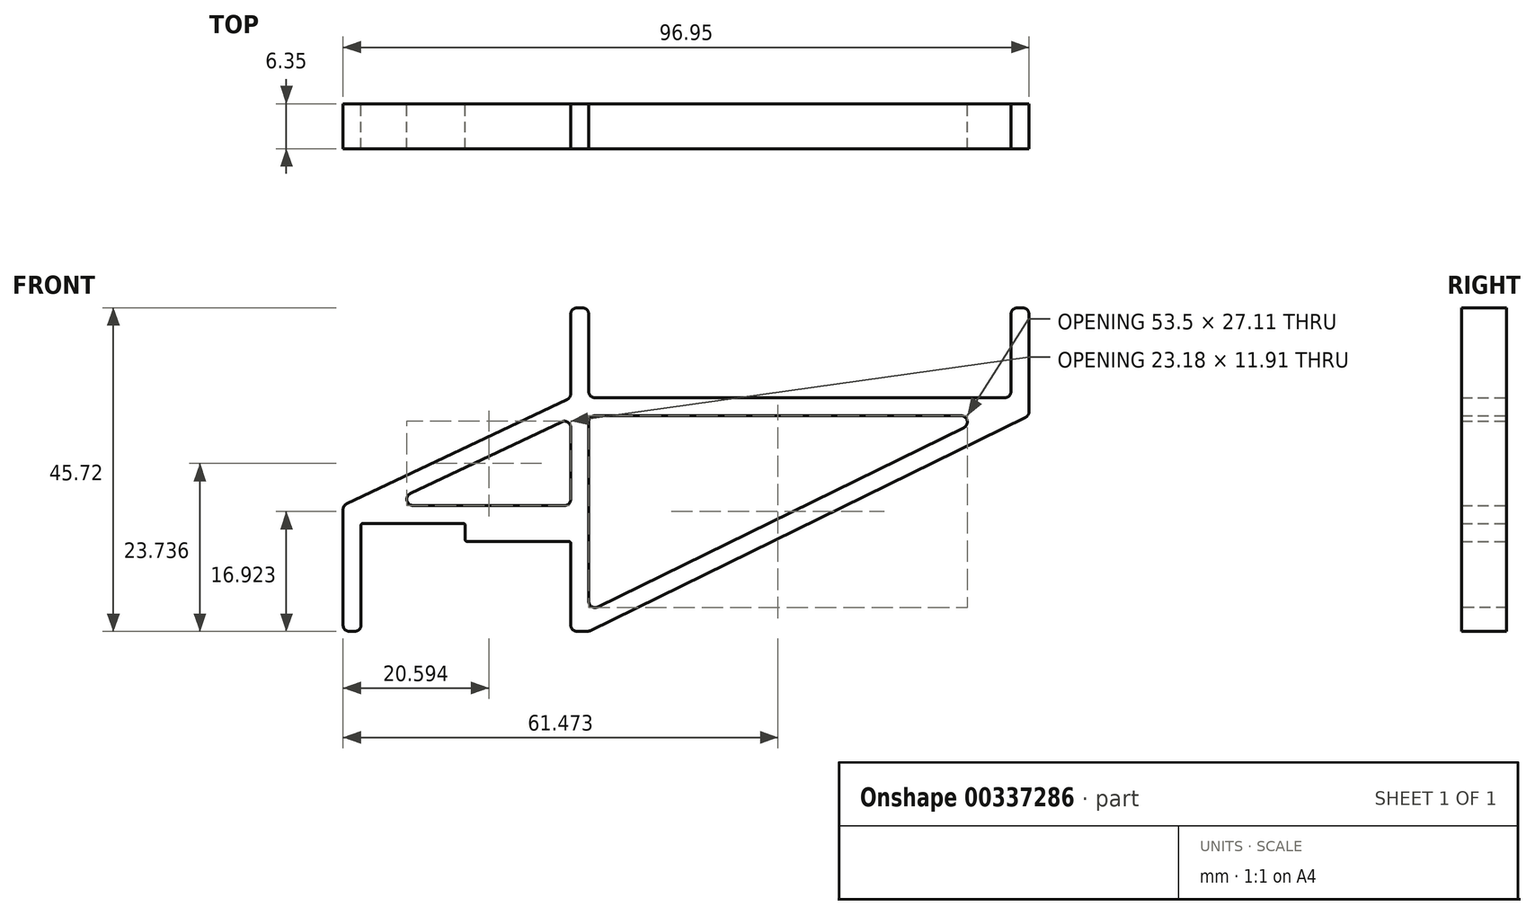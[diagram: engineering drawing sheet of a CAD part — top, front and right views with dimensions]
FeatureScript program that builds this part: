
annotation { "Feature Type Name" : "Feature", "Feature Type Description" : "" }
export const myFeature = defineFeature(function(context is Context, id is Id, definition is map)
    precondition{}
    {
        {
            var Q0;
            Q0=qCreatedBy(makeId("Front.planeOp"),FACE);
            var sketch = newSketch(context, id + "F0", { "sketchPlane" : qUnion([Q0])});
            skLineSegment(sketch, "E0", {"start": v(2.54, 17.78) * mm, "end": v(2.54, 15.24) * mm});
            skLineSegment(sketch, "E1", {"start": v(2.54, 15.24) * mm, "end": v(32.18, 15.24) * mm});
            skLineSegment(sketch, "E2", {"start": v(17.27, 15.24) * mm, "end": v(17.27, 12.7) * mm});
            skLineSegment(sketch, "E3", {"start": v(2.54, 17.78) * mm, "end": v(32.18, 17.78) * mm});
            skLineSegment(sketch, "E4", {"start": v(17.27, 12.7) * mm, "end": v(32.18, 12.7) * mm});
            skLineSegment(sketch, "E5", {"start": v(32.18, 12.7) * mm, "end": v(32.18, 17.78) * mm});
            skLineSegment(sketch, "E6", {"start": v(32.18, 17.78) * mm, "end": v(34.72, 17.78) * mm});
            skLineSegment(sketch, "E7", {"start": v(34.72, 17.78) * mm, "end": v(34.72, 0) * mm});
            skLineSegment(sketch, "E8", {"start": v(32.18, 12.7) * mm, "end": v(32.18, 0) * mm});
            skLineSegment(sketch, "E9", {"start": v(2.54, 17.78) * mm, "end": v(0, 17.78) * mm});
            skLineSegment(sketch, "E10", {"start": v(2.54, 15.24) * mm, "end": v(2.54, 0) * mm});
            skLineSegment(sketch, "E11", {"start": v(0, 17.78) * mm, "end": v(0, 0) * mm});
            skLineSegment(sketch, "E12", {"start": v(0, 0) * mm, "end": v(2.54, 0) * mm});
            skLineSegment(sketch, "E13", {"start": v(34.72, 17.78) * mm, "end": v(34.72, 13.97) * mm});
            skLineSegment(sketch, "E14", {"start": v(32.18, 0) * mm, "end": v(34.72, 0) * mm});
            skLineSegment(sketch, "E15", {"start": v(32.18, 17.78) * mm, "end": v(32.18, 20.32) * mm});
            skLineSegment(sketch, "E16", {"start": v(32.18, 20.32) * mm, "end": v(32.18, 33.02) * mm});
            skLineSegment(sketch, "E17", {"start": v(32.18, 33.02) * mm, "end": v(34.72, 33.02) * mm});
            skLineSegment(sketch, "E18", {"start": v(0, 17.78) * mm, "end": v(32.18, 33.02) * mm});
            skLineSegment(sketch, "E19", {"start": v(5.93, 17.78) * mm, "end": v(32.18, 30.2) * mm});
            skLineSegment(sketch, "E20", {"start": v(34.72, 33.02) * mm, "end": v(34.72, 17.78) * mm});
            skLineSegment(sketch, "E21", {"start": v(34.72, 33.02) * mm, "end": v(96.95, 33.02) * mm});
            skLineSegment(sketch, "E22", {"start": v(96.95, 33.02) * mm, "end": v(96.95, 30.48) * mm});
            skLineSegment(sketch, "E23", {"start": v(34.72, 30.48) * mm, "end": v(96.95, 30.48) * mm});
            skLineSegment(sketch, "E24", {"start": v(32.18, 33.02) * mm, "end": v(32.18, 45.72) * mm});
            skLineSegment(sketch, "E25", {"start": v(32.18, 45.72) * mm, "end": v(34.72, 45.72) * mm});
            skLineSegment(sketch, "E26", {"start": v(34.72, 33.02) * mm, "end": v(34.72, 45.72) * mm});
            skLineSegment(sketch, "E27", {"start": v(96.95, 33.02) * mm, "end": v(96.95, 45.72) * mm});
            skLineSegment(sketch, "E28", {"start": v(96.95, 45.72) * mm, "end": v(94.41, 45.72) * mm});
            skLineSegment(sketch, "E29", {"start": v(94.41, 45.72) * mm, "end": v(94.41, 33.02) * mm});
            skLineSegment(sketch, "E30", {"start": v(34.72, 0) * mm, "end": v(96.95, 30.48) * mm});
            skLineSegment(sketch, "E31", {"start": v(34.72, 2.83) * mm, "end": v(91.18, 30.48) * mm});
            skSolve(sketch);
        }
        {
            var Q0;
            {var subQ0=sQuery(id+"F0.wireOp",EDGE,"jvLbMz3n-FQXq-gv2P-DcQT-8QfjgkFX3igj");Q0=makeQuery(id+"F0.imprint","IMPRINT",FACE,{"disambiguationData":[TD([[makeQuery(id+"F0.imprint","IMPRINT",EDGE,{"derivedFrom":subQ0}),1.0]])]});}
            var Q1;
            {var subQ4=sQuery(id+"F0.wireOp",EDGE,"E6");Q1=makeQuery(id+"F0.imprint","IMPRINT",FACE,{"disambiguationData":[TD([[makeQuery(id+"F0.imprint","IMPRINT",EDGE,{"derivedFrom":subQ4}),1.0]])]});}
            var Q2;
            {var subQ0=sQuery(id+"F0.wireOp",EDGE,"5fyH0i7X-IWu1-a1HD-RHR6-HmbiZMtqhNbi");Q2=makeQuery(id+"F0.imprint","IMPRINT",FACE,{"disambiguationData":[TD([[makeQuery(id+"F0.imprint","IMPRINT",EDGE,{"derivedFrom":subQ0}),-1.0]])]});}
            var Q3;
            {var subQ3=sQuery(id+"F0.wireOp",EDGE,"E6");Q3=makeQuery(id+"F0.imprint","IMPRINT",FACE,{"disambiguationData":[TD([[makeQuery(id+"F0.imprint","IMPRINT",EDGE,{"derivedFrom":subQ3}),-1.0]])]});}
            var Q4;
            {var subQ0=sQuery(id+"F0.wireOp",EDGE,"E17");Q4=makeQuery(id+"F0.imprint","IMPRINT",FACE,{"disambiguationData":[TD([[makeQuery(id+"F0.imprint","IMPRINT",EDGE,{"derivedFrom":subQ0}),-1.0]])]});}
            var Q5;
            {var subQ1=sQuery(id+"F0.wireOp",EDGE,"E9");Q5=makeQuery(id+"F0.imprint","IMPRINT",FACE,{"disambiguationData":[TD([[makeQuery(id+"F0.imprint","IMPRINT",EDGE,{"derivedFrom":subQ1}),-1.0]])]});}
            var Q6;
            {var subQ1=sQuery(id+"F0.wireOp",EDGE,"E0");Q6=makeQuery(id+"F0.imprint","IMPRINT",FACE,{"disambiguationData":[TD([[makeQuery(id+"F0.imprint","IMPRINT",EDGE,{"derivedFrom":subQ1}),1.0]])]});}
            var Q7;
            {var subQ3=sQuery(id+"F0.wireOp",EDGE,"E2");Q7=makeQuery(id+"F0.imprint","IMPRINT",FACE,{"disambiguationData":[TD([[makeQuery(id+"F0.imprint","IMPRINT",EDGE,{"derivedFrom":subQ3}),1.0]])]});}
            var Q8;
            Q8=makeQuery(id+"F0.imprint","IMPRINT",FACE,{"disambiguationData":[TD([[makeQuery(id+"F0.imprint","IMPRINT",EDGE,{"derivedFrom":sQuery(id+"F0.wireOp",EDGE,"E0")}),-1.0]])]});
            var Q9;
            {var subQ0=sQuery(id+"F0.wireOp",EDGE,"E30");Q9=makeQuery(id+"F0.imprint","IMPRINT",FACE,{"disambiguationData":[TD([[makeQuery(id+"F0.imprint","IMPRINT",EDGE,{"derivedFrom":subQ0}),1.0]])]});}
            var Q10;
            {var subQ0=sQuery(id+"F0.wireOp",EDGE,"E22");Q10=makeQuery(id+"F0.imprint","IMPRINT",FACE,{"disambiguationData":[TD([[makeQuery(id+"F0.imprint","IMPRINT",EDGE,{"derivedFrom":subQ0}),-1.0]])]});}
            var Q11;
            {var subQ0=sQuery(id+"F0.wireOp",EDGE,"E27");Q11=makeQuery(id+"F0.imprint","IMPRINT",FACE,{"disambiguationData":[TD([[makeQuery(id+"F0.imprint","IMPRINT",EDGE,{"derivedFrom":subQ0}),1.0]])]});}
            var Q12;
            Q12=makeQuery(id+"F0.imprint","IMPRINT",FACE,{"disambiguationData":[TD([[makeQuery(id+"F0.imprint","IMPRINT",EDGE,{"derivedFrom":sQuery(id+"F0.wireOp",EDGE,"E17")}),1.0]])]});
            extrude(context, id + "F1", {"entities" : qUnion([Q0, Q1, Q2, Q3, Q4, Q5, Q6, Q7, Q8, Q9, Q10, Q11, Q12]), "depth" : 6.35 * mm, "offsetDistance" : 25.4 * mm});
        }
        {
            var Q0;
            Q0=makeQuery(id+"F1.opExtrude","SWEPT_EDGE",EDGE,{"disambiguationData":[OSD([sQuery(id+"F0.wireOp",EDGE,"E11"),sQuery(id+"F0.wireOp",EDGE,"E12")])]});
            var Q1;
            Q1=makeQuery(id+"F1.opExtrude","SWEPT_EDGE",EDGE,{"disambiguationData":[OSD([sQuery(id+"F0.wireOp",EDGE,"E10"),sQuery(id+"F0.wireOp",EDGE,"E12")])]});
            var Q2;
            Q2=makeQuery(id+"F1.opExtrude","SWEPT_EDGE",EDGE,{"disambiguationData":[OSD([sQuery(id+"F0.wireOp",EDGE,"E8"),sQuery(id+"F0.wireOp",EDGE,"E14")])]});
            var Q3;
            Q3=makeQuery(id+"F1.opExtrude","SWEPT_EDGE",EDGE,{"disambiguationData":[OSD([sQuery(id+"F0.wireOp",EDGE,"E7"),sQuery(id+"F0.wireOp",EDGE,"E14"),sQuery(id+"F0.wireOp",EDGE,"5fyH0i7X-IWu1-a1HD-RHR6-HmbiZMtqhNbi")])]});
            var Q4;
            Q4=makeQuery(id+"F1.opExtrude","SWEPT_EDGE",EDGE,{"disambiguationData":[OSD([sQuery(id+"F0.wireOp",EDGE,"XK4gZvIV-EjMV-5yAQ-Ko4O-cfLP38Z1F7WN"),sQuery(id+"F0.wireOp",EDGE,"7Lkjueb4-pT6m-45AM-mPG1-UAD8002npaEU"),sQuery(id+"F0.wireOp",EDGE,"5fyH0i7X-IWu1-a1HD-RHR6-HmbiZMtqhNbi")])]});
            var Q5;
            Q5=makeQuery(id+"F1.opExtrude","SWEPT_EDGE",EDGE,{"disambiguationData":[OSD([sQuery(id+"F0.wireOp",EDGE,"jvLbMz3n-FQXq-gv2P-DcQT-8QfjgkFX3igj"),sQuery(id+"F0.wireOp",EDGE,"qnbmaB5V-popD-AF3a-DfRj-HsTCZiOA8s9y")])]});
            var Q6;
            Q6=makeQuery(id+"F1.opExtrude","SWEPT_EDGE",EDGE,{"disambiguationData":[OSD([sQuery(id+"F0.wireOp",EDGE,"qnbmaB5V-popD-AF3a-DfRj-HsTCZiOA8s9y"),sQuery(id+"F0.wireOp",EDGE,"aIP8VWIh-LyoE-sRiJ-CMpf-Z2WFARpvebgj")])]});
            var Q7;
            Q7=makeQuery(id+"F1.opExtrude","SWEPT_EDGE",EDGE,{"disambiguationData":[OSD([sQuery(id+"F0.wireOp",EDGE,"6lxfTYoy-XcvB-1Uv5-WnG9-A3RQKU2m3VZt"),sQuery(id+"F0.wireOp",EDGE,"aIP8VWIh-LyoE-sRiJ-CMpf-Z2WFARpvebgj")])]});
            var Q8;
            Q8=makeQuery(id+"F1.opExtrude","SWEPT_EDGE",EDGE,{"disambiguationData":[OSD([sQuery(id+"F0.wireOp",EDGE,"6lxfTYoy-XcvB-1Uv5-WnG9-A3RQKU2m3VZt"),sQuery(id+"F0.wireOp",EDGE,"DMFJkJL7-YD1f-RirW-OZ3E-zvg2S2j0YXvj")])]});
            var Q9;
            Q9=makeQuery(id+"F1.opExtrude","SWEPT_EDGE",EDGE,{"disambiguationData":[OSD([sQuery(id+"F0.wireOp",EDGE,"E17"),sQuery(id+"F0.wireOp",EDGE,"DMFJkJL7-YD1f-RirW-OZ3E-zvg2S2j0YXvj")])]});
            var Q10;
            Q10=makeQuery(id+"F1.opExtrude","SWEPT_EDGE",EDGE,{"disambiguationData":[OSD([sQuery(id+"F0.wireOp",EDGE,"E16"),sQuery(id+"F0.wireOp",EDGE,"E17"),sQuery(id+"F0.wireOp",EDGE,"E18")])]});
            var Q11;
            Q11=makeQuery(id+"F1.opExtrude","SWEPT_EDGE",EDGE,{"disambiguationData":[OSD([sQuery(id+"F0.wireOp",EDGE,"E9"),sQuery(id+"F0.wireOp",EDGE,"E11"),sQuery(id+"F0.wireOp",EDGE,"E18")])]});
            var Q12;
            Q12=makeQuery(id+"F1.opExtrude","SWEPT_EDGE",EDGE,{"disambiguationData":[OSD([sQuery(id+"F0.wireOp",EDGE,"E3"),sQuery(id+"F0.wireOp",EDGE,"E5"),sQuery(id+"F0.wireOp",EDGE,"E6"),sQuery(id+"F0.wireOp",EDGE,"E15")])]});
            var Q13;
            Q13=makeQuery(id+"F1.opExtrude","SWEPT_EDGE",EDGE,{"disambiguationData":[OSD([sQuery(id+"F0.wireOp",EDGE,"E16"),sQuery(id+"F0.wireOp",EDGE,"E19")])]});
            var Q14;
            Q14=makeQuery(id+"F1.opExtrude","SWEPT_EDGE",EDGE,{"disambiguationData":[OSD([sQuery(id+"F0.wireOp",EDGE,"E3"),sQuery(id+"F0.wireOp",EDGE,"E19")])]});
            var Q15;
            Q15=makeQuery(id+"F1.opExtrude","SWEPT_EDGE",EDGE,{"disambiguationData":[OSD([sQuery(id+"F0.wireOp",EDGE,"E6"),sQuery(id+"F0.wireOp",EDGE,"E13"),sQuery(id+"F0.wireOp",EDGE,"XK4gZvIV-EjMV-5yAQ-Ko4O-cfLP38Z1F7WN")])]});
            var Q16;
            Q16=makeQuery(id+"F1.opExtrude","SWEPT_EDGE",EDGE,{"disambiguationData":[OSD([sQuery(id+"F0.wireOp",EDGE,"XK4gZvIV-EjMV-5yAQ-Ko4O-cfLP38Z1F7WN"),sQuery(id+"F0.wireOp",EDGE,"Zk52e19d-0mzT-GTo3-gYqh-DDcSyQSH87MV")])]});
            var Q17;
            Q17=makeQuery(id+"F1.opExtrude","SWEPT_EDGE",EDGE,{"disambiguationData":[OSD([sQuery(id+"F0.wireOp",EDGE,"E7"),sQuery(id+"F0.wireOp",EDGE,"Zk52e19d-0mzT-GTo3-gYqh-DDcSyQSH87MV")])]});
            var Q18;
            Q18=makeQuery(id+"F1.opExtrude","SWEPT_EDGE",EDGE,{"disambiguationData":[OSD([sQuery(id+"F0.wireOp",EDGE,"E20"),sQuery(id+"F0.wireOp",EDGE,"E23")])]});
            var Q19;
            Q19=makeQuery(id+"F1.opExtrude","SWEPT_EDGE",EDGE,{"disambiguationData":[OSD([sQuery(id+"F0.wireOp",EDGE,"E23"),sQuery(id+"F0.wireOp",EDGE,"E31")])]});
            var Q20;
            Q20=makeQuery(id+"F1.opExtrude","SWEPT_EDGE",EDGE,{"disambiguationData":[OSD([sQuery(id+"F0.wireOp",EDGE,"E22"),sQuery(id+"F0.wireOp",EDGE,"E23"),sQuery(id+"F0.wireOp",EDGE,"E30")])]});
            var Q21;
            Q21=makeQuery(id+"F1.opExtrude","SWEPT_EDGE",EDGE,{"disambiguationData":[OSD([sQuery(id+"F0.wireOp",EDGE,"E27"),sQuery(id+"F0.wireOp",EDGE,"E28")])]});
            var Q22;
            Q22=makeQuery(id+"F1.opExtrude","SWEPT_EDGE",EDGE,{"disambiguationData":[OSD([sQuery(id+"F0.wireOp",EDGE,"E28"),sQuery(id+"F0.wireOp",EDGE,"E29")])]});
            var Q23;
            Q23=makeQuery(id+"F1.opExtrude","SWEPT_EDGE",EDGE,{"disambiguationData":[OSD([sQuery(id+"F0.wireOp",EDGE,"E21"),sQuery(id+"F0.wireOp",EDGE,"E29")])]});
            var Q24;
            Q24=makeQuery(id+"F1.opExtrude","SWEPT_EDGE",EDGE,{"disambiguationData":[OSD([sQuery(id+"F0.wireOp",EDGE,"E24"),sQuery(id+"F0.wireOp",EDGE,"E25")])]});
            var Q25;
            Q25=makeQuery(id+"F1.opExtrude","SWEPT_EDGE",EDGE,{"disambiguationData":[OSD([sQuery(id+"F0.wireOp",EDGE,"E25"),sQuery(id+"F0.wireOp",EDGE,"E26")])]});
            fillet(context, id + "F2", {"entities" : qUnion([Q0, Q1, Q2, Q3, Q4, Q5, Q6, Q7, Q8, Q9, Q10, Q11, Q12, Q13, Q14, Q15, Q16, Q17, Q18, Q19, Q20, Q21, Q22, Q23, Q24, Q25]), "tangentPropagation" : true, "radius" : 0.89 * mm, "defaultsChanged" : false, "vertexSettings" : [], "allowEdgeOverflow" : false});
        }
        {
            var Q0;
            Q0=makeQuery(id+"F1.opExtrude","SWEPT_EDGE",EDGE,{"disambiguationData":[OSD([sQuery(id+"F0.wireOp",EDGE,"E0"),sQuery(id+"F0.wireOp",EDGE,"E1"),sQuery(id+"F0.wireOp",EDGE,"E10")])]});
            var Q1;
            Q1=makeQuery(id+"F1.opExtrude","SWEPT_EDGE",EDGE,{"disambiguationData":[OSD([sQuery(id+"F0.wireOp",EDGE,"E1"),sQuery(id+"F0.wireOp",EDGE,"E2")])]});
            var Q2;
            Q2=makeQuery(id+"F1.opExtrude","SWEPT_EDGE",EDGE,{"disambiguationData":[OSD([sQuery(id+"F0.wireOp",EDGE,"E2"),sQuery(id+"F0.wireOp",EDGE,"E4")])]});
            var Q3;
            Q3=makeQuery(id+"F1.opExtrude","SWEPT_EDGE",EDGE,{"disambiguationData":[OSD([sQuery(id+"F0.wireOp",EDGE,"E4"),sQuery(id+"F0.wireOp",EDGE,"E5"),sQuery(id+"F0.wireOp",EDGE,"E8")])]});
            fillet(context, id + "F3", {"entities" : qUnion([Q0, Q1, Q2, Q3]), "tangentPropagation" : true, "radius" : 0.25 * mm, "defaultsChanged" : true, "vertexSettings" : [], "allowEdgeOverflow" : false});
        }
    });
